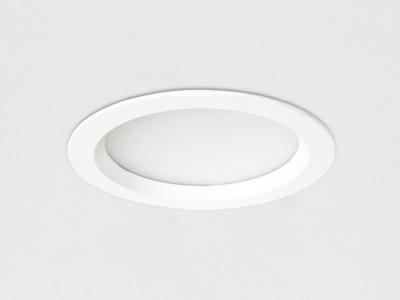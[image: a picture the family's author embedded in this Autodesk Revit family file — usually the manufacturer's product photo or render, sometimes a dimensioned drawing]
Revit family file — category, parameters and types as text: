
# Revit family: DG 1016 MON+
name_source: partatom
category: Lighting Fixtures
revit_build: Autodesk Revit 2017 (Build: 20160225_1515(x64)
units: mm (PartAtom-declared; Revit-internal decimal feet)

## family parameters
Always vertical = Yes
Cut with Voids When Loaded = No
Host = Ceiling
Light Source = Yes
OmniClass Number = 23.80.70.11
OmniClass Title = Luminaries for Internal Lighting
Part Type = Normal
Room Calculation Point = No
Round Connector Dimension = Use Diameter
Shared = No

## types (2) — shared parameters
Apparent Load = 11 VA
Color Filter = 16777215
Dimming Lamp Color Temperature Shift = <None>
Emit Shape Visible in Rendering = Yes
Emit from Circle Diameter = 120 mm  [stored 0.393701 ft]
Light Source Symbol Size = 610 mm
Manufacturer = ARLIGHT
Type Comments = MON+
Type Image = DG 1016 MON.jpg
Wattage Comments = 11W

## type names (no varying parameters)
- DGMON+.160.11.30
- DGMON+.160.11.40

note: [stored X ft] marks values corroborated as IEEE doubles in the binary element streams (Revit-internal decimal feet)

## geometry (parser evidence)
native form markers: Sweep x2
no freeform markers — native parametric forms only
